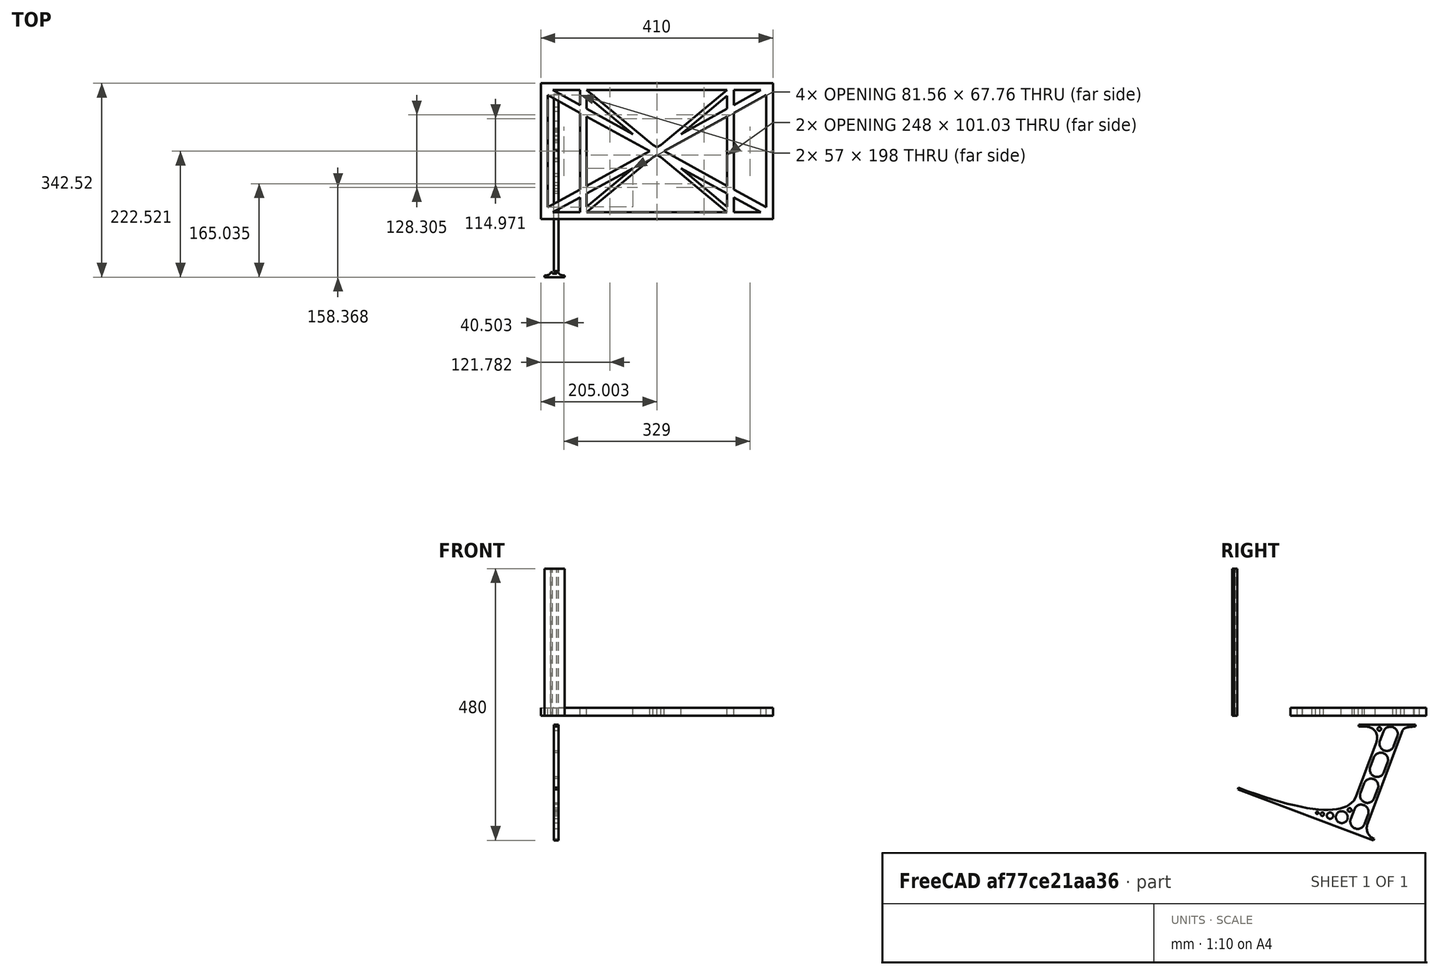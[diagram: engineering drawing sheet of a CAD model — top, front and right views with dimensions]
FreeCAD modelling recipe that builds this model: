
FCSTD DOCUMENT  (FreeCAD 0.19R0.19.2)
Label: laptopStand040
License: All rights reserved
LicenseURL: http://en.wikipedia.org/wiki/All_rights_reserved
objects: Part::Extrusion×4, Sketcher::SketchObject×3
note: 7 computed .brp shape members not serialized (recipe doc carries the construction recipe); baked Part::Feature solids carry a one-line shape summary decoded from their .brp

FEATURE [Sketcher::SketchObject] Sketch
  FullyConstrained = true
  sketch-geometry (52):
    g0: LineSegment StartX=-22.9272 StartY=136.221 StartZ=0 EndX=-22.9272 EndY=-103.779 EndZ=0
    g1: LineSegment StartX=-22.9272 StartY=136.221 StartZ=0 EndX=387.073 EndY=136.221 EndZ=0
    g2: LineSegment StartX=-22.9272 StartY=-103.779 StartZ=0 EndX=387.073 EndY=-103.779 EndZ=0
    g3: LineSegment StartX=387.073 StartY=136.221 StartZ=0 EndX=387.073 EndY=-103.779 EndZ=0
    g4: LineSegment StartX=375.073 StartY=115.221 StartZ=0 EndX=318.073 EndY=83.9235 EndZ=0
    g5: LineSegment StartX=-10.9272 StartY=-82.7794 StartZ=0 EndX=46.0728 EndY=-51.4823 EndZ=0
    g6: LineSegment StartX=-1.92719 StartY=124.221 StartZ=0 EndX=46.0728 EndY=97.8651 EndZ=0
    g7: LineSegment StartX=366.073 StartY=-91.7794 StartZ=0 EndX=318.073 EndY=-65.424 EndZ=0
    g8: LineSegment StartX=-10.9272 StartY=115.221 StartZ=0 EndX=-10.9272 EndY=-82.7794 EndZ=0
    g9: LineSegment StartX=375.073 StartY=-82.7794 StartZ=0 EndX=375.073 EndY=115.221 EndZ=0
    g10: LineSegment StartX=-1.92719 StartY=-91.7794 StartZ=0 EndX=46.0728 EndY=-91.7794 EndZ=0
    g11: LineSegment StartX=318.073 StartY=124.221 StartZ=0 EndX=366.073 EndY=124.221 EndZ=0
    g12: LineSegment StartX=306.073 StartY=-81.8102 StartZ=0 EndX=224.513 EndY=-14.0532 EndZ=0
    g13: LineSegment StartX=58.0728 StartY=114.251 StartZ=0 EndX=139.632 EndY=46.4944 EndZ=0
    g14: LineSegment StartX=306.073 StartY=124.221 StartZ=0 EndX=189.124 EndY=27.0628 EndZ=0
    g15: LineSegment StartX=58.0728 StartY=-91.7794 StartZ=0 EndX=175.022 EndY=5.37834 EndZ=0
    g16: LineSegment StartX=46.0728 StartY=124.221 StartZ=0 EndX=46.0728 EndY=97.8651 EndZ=0
    g17: LineSegment StartX=58.0728 StartY=-81.8102 StartZ=0 EndX=58.0728 EndY=-58.8351 EndZ=0
    g18: LineSegment StartX=318.073 StartY=124.221 StartZ=0 EndX=318.073 EndY=97.8651 EndZ=0
    g19: LineSegment StartX=306.073 StartY=114.251 StartZ=0 EndX=306.073 EndY=91.2763 EndZ=0
    g20: LineSegment StartX=182.073 StartY=23.1914 StartZ=0 EndX=189.124 EndY=27.0628 EndZ=0
    g21: LineSegment StartX=182.073 StartY=9.24976 StartZ=0 EndX=175.022 EndY=5.37834 EndZ=0
    g22: LineSegment StartX=224.513 StartY=46.4944 StartZ=0 EndX=306.073 EndY=114.251 EndZ=0
    g23: LineSegment StartX=175.022 StartY=27.0628 StartZ=0 EndX=58.0728 EndY=124.221 EndZ=0
    g24: LineSegment StartX=169.377 StartY=16.2206 StartZ=0 EndX=58.0728 EndY=77.3346 EndZ=0
    g25: LineSegment StartX=139.632 StartY=-14.0532 StartZ=0 EndX=58.0728 EndY=-81.8102 EndZ=0
    g26: LineSegment StartX=194.768 StartY=16.2206 StartZ=0 EndX=306.073 EndY=-44.8935 EndZ=0
    g27: LineSegment StartX=224.513 StartY=46.4944 StartZ=0 EndX=306.073 EndY=91.2763 EndZ=0
    g28: LineSegment StartX=175.022 StartY=27.0628 StartZ=0 EndX=182.073 EndY=23.1914 EndZ=0
    g29: LineSegment StartX=139.632 StartY=-14.0532 StartZ=0 EndX=58.0728 EndY=-58.8351 EndZ=0
    g30: LineSegment StartX=189.124 StartY=5.37834 StartZ=0 EndX=182.073 EndY=9.24976 EndZ=0
    g31: LineSegment StartX=189.124 StartY=5.37834 StartZ=0 EndX=306.073 EndY=-91.7794 EndZ=0
    g32: LineSegment StartX=306.073 StartY=77.3346 StartZ=0 EndX=306.073 EndY=-44.8935 EndZ=0
    g33: LineSegment StartX=318.073 StartY=83.9235 StartZ=0 EndX=318.073 EndY=-51.4823 EndZ=0
    g34: LineSegment StartX=318.073 StartY=97.8651 StartZ=0 EndX=366.073 EndY=124.221 EndZ=0
    g35: LineSegment StartX=306.073 StartY=77.3346 StartZ=0 EndX=194.768 EndY=16.2206 EndZ=0
    g36: LineSegment StartX=306.073 StartY=-58.8351 StartZ=0 EndX=224.513 EndY=-14.0532 EndZ=0
    g37: LineSegment StartX=306.073 StartY=-58.8351 StartZ=0 EndX=306.073 EndY=-81.8102 EndZ=0
    g38: LineSegment StartX=318.073 StartY=-51.4823 StartZ=0 EndX=375.073 EndY=-82.7794 EndZ=0
    g39: LineSegment StartX=318.073 StartY=-65.424 StartZ=0 EndX=318.073 EndY=-91.7794 EndZ=0
    g40: LineSegment StartX=306.073 StartY=124.221 StartZ=0 EndX=58.0728 EndY=124.221 EndZ=0
    g41: LineSegment StartX=318.073 StartY=-91.7794 StartZ=0 EndX=366.073 EndY=-91.7794 EndZ=0
    g42: LineSegment StartX=58.0728 StartY=-91.7794 StartZ=0 EndX=306.073 EndY=-91.7794 EndZ=0
    g43: LineSegment StartX=58.0728 StartY=-44.8935 StartZ=0 EndX=58.0728 EndY=77.3346 EndZ=0
    g44: LineSegment StartX=46.0728 StartY=-65.424 StartZ=0 EndX=-1.92719 EndY=-91.7794 EndZ=0
    g45: LineSegment StartX=46.0728 StartY=-65.424 StartZ=0 EndX=46.0728 EndY=-91.7794 EndZ=0
    g46: LineSegment StartX=58.0728 StartY=-44.8935 StartZ=0 EndX=169.377 EndY=16.2206 EndZ=0
    g47: LineSegment StartX=58.0728 StartY=91.2763 StartZ=0 EndX=58.0728 EndY=114.251 EndZ=0
    g48: LineSegment StartX=46.0728 StartY=83.9235 StartZ=0 EndX=46.0728 EndY=-51.4823 EndZ=0
    g49: LineSegment StartX=46.0728 StartY=124.221 StartZ=0 EndX=-1.92719 EndY=124.221 EndZ=0
    g50: LineSegment StartX=58.0728 StartY=91.2763 StartZ=0 EndX=139.632 EndY=46.4944 EndZ=0
    g51: LineSegment StartX=46.0728 StartY=83.9235 StartZ=0 EndX=-10.9272 EndY=115.221 EndZ=0
  constraints (102):
    c: Vertical(g0)
    c: Distance(g0) = 240
    c: Horizontal(g1)
    c: Distance(g1) = 410
    c: Coincident(g1,g0)
    c: Coincident(g2,g0)
    c: Horizontal(g2)
    c: Coincident(g3,g1)
    c: Vertical(g3)
    c: Coincident(g2,g3)
    c: Block(g1)
    c: Horizontal(g10)
    c: Horizontal(g11)
    c: PointOnObject(g35,g6)
    c: Coincident(g28,g20)
    c: Coincident(g30,g21)
    c: Tangent(g7,g24)
    c: PointOnObject(g24,g5)
    c: PointOnObject(g26,g4)
    c: Coincident(g20,g14)
    c: Tangent(g20,g27)
    c: Coincident(g50,g13)
    c: Coincident(g28,g23)
    c: Coincident(g22,g27)
    c: Coincident(g21,g15)
    c: Coincident(g29,g25)
    c: Tangent(g21,g29)
    c: Coincident(g36,g12)
    c: Coincident(g31,g30)
    c: Coincident(g22,g19)
    c: Tangent(g19,g32)
    c: Tangent(g18,g33)
    c: Coincident(g27,g19)
    c: Tangent(g27,g34)
    c: Coincident(g4,g33)
    c: Coincident(g35,g32)
    c: Tangent(g4,g35)
    c: Coincident(g37,g12)
    c: Tangent(g7,g36)
    c: Tangent(g32,g37)
    c: Coincident(g26,g32)
    c: Tangent(g26,g38)
    c: Coincident(g33,g38)
    c: Coincident(g39,g7)
    c: Tangent(g33,g39)
    c: Coincident(g25,g17)
    c: Tangent(g17,g43)
    c: Coincident(g29,g17)
    c: Tangent(g29,g44)
    c: Coincident(g45,g44)
    c: Tangent(g16,g45)
    c: Coincident(g5,g48)
    c: Coincident(g46,g43)
    c: Tangent(g5,g46)
    c: Tangent(g43,g47)
    c: Tangent(g16,g48)
    c: Coincident(g13,g47)
    c: PointOnObject(g40,g23)
    c: Tangent(g40,g49)
    c: Coincident(g6,g16)
    c: Coincident(g50,g47)
    c: Tangent(g6,g50)
    c: Coincident(g24,g43)
    c: Coincident(g51,g48)
    c: Tangent(g24,g51)
    c: Block(g23)
    c: Block(g14)
    c: Block(g20)
    c: Block(g40)
    c: Block(g18)
    c: Block(g34)
    c: Block(g4)
    c: Block(g38)
    c: Block(g9)
    c: Block(g36)
    c: Block(g37)
    c: Block(g7)
    c: Block(g39)
    c: Block(g22)
    c: Block(g31)
    c: Block(g42)
    c: Block(g21)
    c: Block(g15)
    c: Block(g29)
    c: Block(g25)
    c: Block(g45)
    c: Block(g44)
    c: Block(g5)
    c: Block(g8)
    c: Block(g51)
    c: Block(g6)
    c: Block(g16)
    c: Block(g13)
    c: Block(g47)
    c: Block(g35)
    c: Block(g32)
    c: Block(g24)
    c: Block(g46)
    c: Block(g49)
    c: Block(g11)
    c: Block(g41)
    c: Block(g10)
FEATURE [Sketcher::SketchObject] Sketch001
  FullyConstrained = true
  MapMode = 4
  Placement = pos=(0,0,0) rot=(0.57735,0.57735,0.57735;2.0944rad)
  Support = -> [Sketch]
  sketch-geometry (46):
    g0: BSplineCurve PolesCount=3 KnotsCount=2 Degree=2 IsPeriodic=0
    g1: ArcOfCircle CenterX=73.122 CenterY=-32.2909 CenterZ=0 NormalX=0 NormalY=0 NormalZ=1 AngleXU=0 Radius=13 StartAngle=5.92268 EndAngle=9.06428
    g2: ArcOfCircle CenterX=66.7816 CenterY=-49.1439 CenterZ=0 NormalX=0 NormalY=0 NormalZ=1 AngleXU=0 Radius=13 StartAngle=2.78068 EndAngle=5.92131
    g3: ArcOfCircle CenterX=55.9263 CenterY=-78.1807 CenterZ=0 NormalX=0 NormalY=0 NormalZ=1 AngleXU=0 Radius=13 StartAngle=5.92268 EndAngle=9.06428
    g4: ArcOfCircle CenterX=49.5884 CenterY=-95.0342 CenterZ=0 NormalX=0 NormalY=0 NormalZ=1 AngleXU=0 Radius=13 StartAngle=2.78068 EndAngle=5.92131
    g5: ArcOfCircle CenterX=38.7206 CenterY=-124.067 CenterZ=0 NormalX=0 NormalY=0 NormalZ=1 AngleXU=0 Radius=13 StartAngle=5.92268 EndAngle=9.06428
    g6: ArcOfCircle CenterX=32.3875 CenterY=-140.92 CenterZ=0 NormalX=0 NormalY=0 NormalZ=1 AngleXU=0 Radius=13 StartAngle=2.78068 EndAngle=5.92131
    g7: ArcOfCircle CenterX=21.4715 CenterY=-169.934 CenterZ=0 NormalX=0 NormalY=0 NormalZ=1 AngleXU=0 Radius=13 StartAngle=5.92268 EndAngle=9.06428
    g8: ArcOfCircle CenterX=15.1336 CenterY=-186.787 CenterZ=0 NormalX=0 NormalY=0 NormalZ=1 AngleXU=0 Radius=13 StartAngle=2.78068 EndAngle=5.92131
    g9-g12: Circle x4 (B-spline internal-alignment scaffolding for g13; pole/knot coordinates omitted)
    g13: BSplineCurve PolesCount=4 KnotsCount=2 Degree=3 IsPeriodic=0
    g14: GeomPoint X=28.8094 Y=-19.0875 Z=0
    g15: GeomPoint X=47.0443 Y=-50.4712 Z=0
    g16: Circle CenterX=53.5586 CenterY=-23.2695 CenterZ=0 NormalX=0 NormalY=0 NormalZ=1 AngleXU=0 Radius=3.24518
    g17: Circle CenterX=-195.441 CenterY=-127.082 CenterZ=0 NormalX=0 NormalY=0 NormalZ=1 AngleXU=0 Radius=1
    g18: Circle CenterX=-8.24091 CenterY=-197.481 CenterZ=0 NormalX=0 NormalY=0 NormalZ=1 AngleXU=0 Radius=1
    g19: Circle CenterX=12.8789 CenterY=-141.321 CenterZ=0 NormalX=0 NormalY=0 NormalZ=1 AngleXU=0 Radius=1
    g20: BSplineCurve PolesCount=3 KnotsCount=2 Degree=2 IsPeriodic=0
    g21: GeomPoint X=-195.441 Y=-127.082 Z=0
    g22: GeomPoint X=12.8789 Y=-141.321 Z=0
    g23: Circle CenterX=-12.8016 CenterY=-179.036 CenterZ=0 NormalX=0 NormalY=0 NormalZ=1 AngleXU=0 Radius=10.5072
    g24: Circle CenterX=0.933922 CenterY=-166.43 CenterZ=0 NormalX=0 NormalY=0 NormalZ=1 AngleXU=0 Radius=3.26661
    g25: Circle CenterX=-33.5518 CenterY=-176.44 CenterZ=0 NormalX=0 NormalY=0 NormalZ=1 AngleXU=0 Radius=5.64388
    g26: Circle CenterX=-47.2366 CenterY=-173.859 CenterZ=0 NormalX=0 NormalY=0 NormalZ=1 AngleXU=0 Radius=3.01653
    g27: Circle CenterX=-56.2595 CenterY=-171.456 CenterZ=0 NormalX=0 NormalY=0 NormalZ=1 AngleXU=0 Radius=2.12826
    g28: ArcOfCircle CenterX=51.2151 CenterY=-198.473 CenterZ=0 NormalX=0 NormalY=0 NormalZ=1 AngleXU=0 Radius=20 StartAngle=2.78189 EndAngle=4.35269
    g29: LineSegment StartX=32.4951 StartY=-191.433 StartZ=0 EndX=94.6577 EndY=-26.1351 EndZ=0
    g30: LineSegment StartX=43.1192 StartY=-220.001 StartZ=0 EndX=-196.497 EndY=-129.89 EndZ=0
    g31: LineSegment StartX=43.1192 StartY=-220.001 StartZ=0 EndX=44.1752 EndY=-217.193 EndZ=0
    g32: LineSegment StartX=117.223 StartY=-19.0875 StartZ=0 EndX=117.223 EndY=-16.0875 EndZ=0
    g33: LineSegment StartX=117.223 StartY=-16.0875 StartZ=0 EndX=17.2232 EndY=-16.0875 EndZ=0
    g34: LineSegment StartX=17.2232 StartY=-16.0875 StartZ=0 EndX=17.2232 EndY=-19.0875 EndZ=0
    g35: LineSegment StartX=28.8094 StartY=-19.0875 StartZ=0 EndX=17.2232 EndY=-19.0875 EndZ=0
    g36: LineSegment StartX=47.0443 StartY=-50.4712 StartZ=0 EndX=12.8789 EndY=-141.321 EndZ=0
    g37: LineSegment StartX=-195.441 StartY=-127.082 StartZ=0 EndX=-196.497 EndY=-129.89 EndZ=0
    g38: LineSegment StartX=85.2864 StartY=-36.8765 StartZ=0 EndX=78.9396 EndY=-53.7463 EndZ=0
    g39: LineSegment StartX=60.9577 StartY=-27.7052 StartZ=0 EndX=54.6191 EndY=-44.5532 EndZ=0
    g40: LineSegment StartX=68.0907 StartY=-82.7664 StartZ=0 EndX=61.7465 EndY=-99.6365 EndZ=0
    g41: LineSegment StartX=43.7619 StartY=-73.595 StartZ=0 EndX=37.426 EndY=-90.4435 EndZ=0
    g42: LineSegment StartX=50.885 StartY=-128.652 StartZ=0 EndX=44.5456 EndY=-145.522 EndZ=0
    g43: LineSegment StartX=26.5562 StartY=-119.481 StartZ=0 EndX=20.2251 EndY=-136.329 EndZ=0
    g44: LineSegment StartX=9.3071 StartY=-165.349 StartZ=0 EndX=2.97115 EndY=-182.197 EndZ=0
    g45: LineSegment StartX=33.6358 StartY=-174.52 StartZ=0 EndX=27.2917 EndY=-191.39 EndZ=0
  constraints (70):
    c: Block(g0)
    c: Block(g1)
    c: Block(g2)
    c: Block(g4)
    c: Block(g3)
    c: Block(g6)
    c: Block(g5)
    c: Block(g8)
    c: Block(g7)
    c: Weight(g9) = 1
    c: Equal(g9,g10)
    c: Equal(g9,g11)
    c: Equal(g9,g12)
    c: InternalAlignment(g9-g12 -> g13) x4
    c: InternalAlignment(g14,g13)
    c: InternalAlignment(g15,g13)
    c: Block(g16)
    c: Weight(g17) = 1
    c: Equal(g17,g18)
    c: Equal(g17,g19)
    c: InternalAlignment(g17,g20)
    c: InternalAlignment(g18,g20)
    c: InternalAlignment(g19,g20)
    c: InternalAlignment(g21,g20)
    c: InternalAlignment(g22,g20)
    c: Block(g20)
    c: Block(g23)
    c: Block(g24)
    c: Block(g25)
    c: Block(g26)
    c: Block(g27)
    c: Block(g28)
    c: Coincident(g29,g28)
    c: Coincident(g29,g0)
    c: Block(g13)
    c: Coincident(g31,g30)
    c: Coincident(g31,g28)
    c: Block(g31)
    c: Coincident(g32,g0)
    c: Vertical(g32)
    c: Coincident(g33,g32)
    c: Horizontal(g33)
    c: Coincident(g34,g33)
    c: Vertical(g34)
    c: Block(g33)
    c: Coincident(g35,g13)
    c: Coincident(g35,g34)
    c: Horizontal(g35)
    c: Coincident(g36,g13)
    c: Coincident(g36,g20)
    c: Coincident(g37,g20)
    c: Coincident(g37,g30)
    c: Block(g30)
    c: Coincident(g38,g1)
    c: Coincident(g38,g2)
    c: Coincident(g39,g1)
    c: Coincident(g39,g2)
    c: Coincident(g40,g3)
    c: Coincident(g40,g4)
    c: Coincident(g41,g3)
    c: Coincident(g41,g4)
    c: Coincident(g42,g5)
    c: Coincident(g42,g6)
    c: Coincident(g43,g5)
    c: Coincident(g43,g6)
    c: Coincident(g44,g7)
    c: Coincident(g44,g8)
    c: Coincident(g45,g7)
    c: Coincident(g45,g8)
    c: Distance(g30) = 256
FEATURE [Part::Extrusion] Extrude002
  Base = -> Sketch001
  Dir = (1,0,0)
  DirMode = 2
  FaceMakerClass = Part::FaceMakerBullseye
  LengthFwd = 8
  LengthRev = 0
  Solid = true
  Symmetric = false
FEATURE [Sketcher::SketchObject] Sketch002
  FullyConstrained = true
  sketch-geometry (20):
    g0: LineSegment StartX=-2.77179 StartY=-200.304 StartZ=0 EndX=5.22821 EndY=-200.304 EndZ=0
    g1: LineSegment StartX=5.22821 StartY=-200.304 StartZ=0 EndX=5.22821 EndY=-197.304 EndZ=0
    g2: LineSegment StartX=-2.77179 StartY=-200.304 StartZ=0 EndX=-2.77179 EndY=-197.304 EndZ=0
    g3: LineSegment StartX=5.22821 StartY=-197.304 StartZ=0 EndX=8.22821 EndY=-197.304 EndZ=0
    g4: LineSegment StartX=-2.77179 StartY=-197.304 StartZ=0 EndX=-5.77179 EndY=-197.304 EndZ=0
    g5: LineSegment StartX=19.2282 StartY=-203.304 StartZ=0 EndX=19.2282 EndY=-206.304 EndZ=0
    g6: LineSegment StartX=-16.7718 StartY=-203.304 StartZ=0 EndX=-16.7718 EndY=-206.304 EndZ=0
    g7: LineSegment StartX=-16.7718 StartY=-206.304 StartZ=0 EndX=19.2282 EndY=-206.304 EndZ=0
    g8: Circle CenterX=-16.7718 CenterY=-203.304 CenterZ=0 NormalX=0 NormalY=0 NormalZ=1 AngleXU=0 Radius=1
    g9: Circle CenterX=-5.77179 CenterY=-203.304 CenterZ=0 NormalX=0 NormalY=0 NormalZ=1 AngleXU=0 Radius=1
    g10: Circle CenterX=-5.77179 CenterY=-197.304 CenterZ=0 NormalX=0 NormalY=0 NormalZ=1 AngleXU=0 Radius=1
    g11: BSplineCurve PolesCount=3 KnotsCount=2 Degree=2 IsPeriodic=0
    g12: GeomPoint X=-16.7718 Y=-203.304 Z=0
    g13: GeomPoint X=-5.77179 Y=-197.304 Z=0
    g14: Circle CenterX=19.2282 CenterY=-203.304 CenterZ=0 NormalX=0 NormalY=0 NormalZ=1 AngleXU=0 Radius=1
    g15: Circle CenterX=8.22821 CenterY=-203.304 CenterZ=0 NormalX=0 NormalY=0 NormalZ=1 AngleXU=0 Radius=1
    g16: Circle CenterX=8.22821 CenterY=-197.304 CenterZ=0 NormalX=0 NormalY=0 NormalZ=1 AngleXU=0 Radius=1
    g17: BSplineCurve PolesCount=3 KnotsCount=2 Degree=2 IsPeriodic=0
    g18: GeomPoint X=19.2282 Y=-203.304 Z=0
    g19: GeomPoint X=8.22821 Y=-197.304 Z=0
  constraints (41):
    c: Horizontal(g0)
    c: Distance(g0) = 8
    c: Coincident(g1,g0)
    c: Vertical(g1)
    c: Distance(g1) = 3
    c: Coincident(g2,g0)
    c: Vertical(g2)
    c: Distance(g2) = 3
    c: Coincident(g3,g1)
    c: Horizontal(g3)
    c: Distance(g3) = 3
    c: Coincident(g4,g2)
    c: Horizontal(g4)
    c: Distance(g4) = 3
    c: Vertical(g5)
    c: Vertical(g6)
    c: Coincident(g7,g6)
    c: Coincident(g7,g5)
    c: Weight(g8) = 1
    c: Equal(g8,g9)
    c: Equal(g8,g10)
    c: Coincident(g11,g4)
    c: InternalAlignment(g8,g11)
    c: InternalAlignment(g9,g11)
    c: InternalAlignment(g10,g11)
    c: InternalAlignment(g12,g11)
    c: InternalAlignment(g13,g11)
    c: Coincident(g17,g5)
    c: Weight(g14) = 1
    c: Equal(g14,g15)
    c: Equal(g14,g16)
    c: Coincident(g17,g3)
    c: InternalAlignment(g14,g17)
    c: InternalAlignment(g15,g17)
    c: InternalAlignment(g16,g17)
    c: InternalAlignment(g18,g17)
    c: InternalAlignment(g19,g17)
    c: Block(g7)
    c: Block(g17)
    c: Block(g11)
    c: Block(g6)
FEATURE [Part::Extrusion] Extrude003
  Base = -> Sketch002
  Dir = (0,0,1)
  DirMode = 2
  FaceMakerClass = Part::FaceMakerBullseye
  LengthFwd = 260
  LengthRev = 0
  Solid = true
  Symmetric = false
FEATURE [Part::Extrusion] Extrude
  Base = -> Sketch
  Dir = (0,0,1)
  DirMode = 2
  FaceMakerClass = Part::FaceMakerBullseye
  LengthFwd = 14
  LengthRev = 0
  Solid = true
  Symmetric = false
FEATURE [Part::Extrusion] Extrude004
  Base = -> Sketch
  Dir = (0,0,1)
  DirMode = 2
  FaceMakerClass = Part::FaceMakerBullseye
  LengthFwd = 14
  LengthRev = 0
  Solid = true
  Symmetric = false
